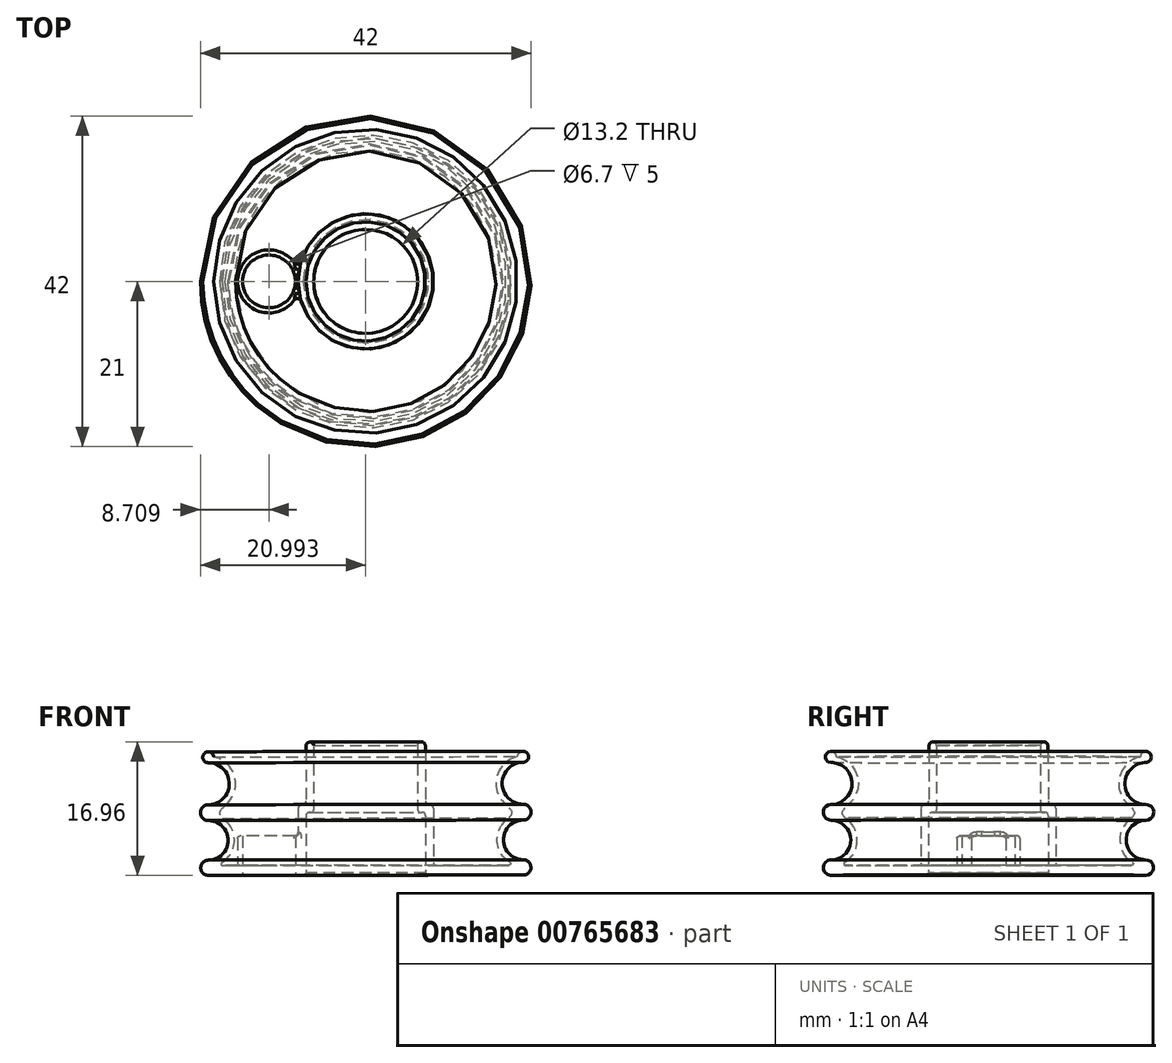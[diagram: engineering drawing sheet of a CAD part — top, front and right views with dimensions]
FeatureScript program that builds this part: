
annotation { "Feature Type Name" : "Feature", "Feature Type Description" : "" }
export const myFeature = defineFeature(function(context is Context, id is Id, definition is map)
    precondition{}
    {
        {
            var Q0;
            Q0=qCreatedBy(makeId("Front.planeOp"),FACE);
            var sketch = newSketch(context, id + "F0", { "sketchPlane" : qUnion([Q0])});
            skLineSegment(sketch, "E0.left", {"start": v(0, 0) * mm, "end": v(-0.02, 15) * mm, "construction": true});
            skLineSegment(sketch, "E0.right", {"start": v(-20, 0) * mm, "end": v(-20.02, 14.31) * mm, "construction": true});
            skLineSegment(sketch, "E1.bottom", {"start": v(-20, 0) * mm, "end": v(-7.61, 0) * mm});
            skLineSegment(sketch, "E1.left", {"start": v(-20, 0) * mm, "end": v(-20.01, 11.57) * mm, "construction": true});
            skLineSegment(sketch, "E2", {"start": v(-7.61, 0) * mm, "end": v(-7.61, 7.57) * mm});
            skPoint(sketch, "E2.endSnap0", {"position": v(-6.61, 7.99) * mm});
            skLineSegment(sketch, "E3", {"start": v(-7.2, 7.99) * mm, "end": v(-6.96, 7.99) * mm});
            skLineSegment(sketch, "E4", {"start": v(-6.62, 16.49) * mm, "end": v(-6.61, 8.34) * mm});
            skArc(sketch, "E5", {"start": v(-20, 0) * mm, "mid": v(-20.97, 0.97) * mm, "end": v(-20, 1.94) * mm});
            skArc(sketch, "E6", {"start": v(-20, 1.94) * mm, "mid": v(-17.5, 4.46) * mm, "end": v(-20, 6.98) * mm});
            skArc(sketch, "E7", {"start": v(-20, 6.98) * mm, "mid": v(-21, 7.97) * mm, "end": v(-20.01, 8.98) * mm});
            skLineSegment(sketch, "E8.4", {"start": v(-7.6, 16.45) * mm, "end": v(-7.6, 9.45) * mm});
            skLineSegment(sketch, "E8.5", {"start": v(-8.15, 8.95) * mm, "end": v(-8.1, 8.95) * mm});
            skLineSegment(sketch, "E8.6", {"start": v(-8.6, 1.25) * mm, "end": v(-8.6, 8.5) * mm});
            skLineSegment(sketch, "E9.0", {"start": v(-19.17, 1.25) * mm, "end": v(-8.6, 1.25) * mm});
            skPoint(sketch, "E10.visualSharp", {"position": v(-7.6, 8.95) * mm});
            skArc(sketch, "E10.filletArc", {"start": v(-8.1, 8.95) * mm, "mid": v(-7.75, 9.1) * mm, "end": v(-7.6, 9.45) * mm});
            skPoint(sketch, "E11.visualSharp", {"position": v(-8.6, 8.95) * mm});
            skArc(sketch, "E11.filletArc", {"start": v(-8.15, 8.95) * mm, "mid": v(-8.47, 8.82) * mm, "end": v(-8.6, 8.5) * mm});
            skArc(sketch, "E12", {"start": v(-20.01, 8.98) * mm, "mid": v(-17.35, 11.65) * mm, "end": v(-20.02, 14.31) * mm});
            skArc(sketch, "E13", {"start": v(-19.32, 15.04) * mm, "mid": v(-20.53, 15.5) * mm, "end": v(-20.02, 14.31) * mm});
            skArc(sketch, "E14.0", {"start": v(-17.85, 8.94) * mm, "mid": v(-16.65, 12.45) * mm, "end": v(-19.32, 15.04) * mm});
            skArc(sketch, "E14.1", {"start": v(-19.17, 1.25) * mm, "mid": v(-16.73, 3.94) * mm, "end": v(-18.22, 7.25) * mm});
            skFitSpline(sketch, "E15", {"points": [v(-17.85, 8.94) * mm, v(-18.6, 7.98) * mm, v(-18.22, 7.25) * mm], "startDerivative": vector(-0.75, -1.37) * mm, "endDerivative": vector(0.7, -1.27) * mm});
            skPoint(sketch, "E16.visualSharp", {"position": v(-7.61, 7.99) * mm});
            skArc(sketch, "E16.filletArc", {"start": v(-7.2, 7.99) * mm, "mid": v(-7.49, 7.86) * mm, "end": v(-7.61, 7.57) * mm});
            skPoint(sketch, "E17.orphan", {"position": v(-6.62, 15.97) * mm});
            skArc(sketch, "E18", {"start": v(-7.6, 16.45) * mm, "mid": v(-7.13, 16.94) * mm, "end": v(-6.62, 16.49) * mm});
            skArc(sketch, "E19.filletArc", {"start": v(-6.96, 7.99) * mm, "mid": v(-6.71, 8.09) * mm, "end": v(-6.61, 8.34) * mm});
            skSolve(sketch);
        }
        {
            var Q0;
            Q0=makeQuery(id+"F0.imprint","IMPRINT",FACE,{"disambiguationData":[TD([[makeQuery(id+"F0.imprint","IMPRINT",EDGE,{"derivedFrom":sQuery(id+"F0.wireOp",EDGE,"E1.bottom")}),1.0]])]});
            var Q1;
            Q1=sQuery(id+"F0.wireOp",EDGE,"E0.left");
            revolve(context, id + "F1", {"surfaceOperationType" : NewSurfaceOperationType.NEW, "entities" : qUnion([Q0]), "axis" : qUnion([Q1]), "revolveType" : RevolveType.FULL});
        }
        {
            var Q0;
            Q0=qCreatedBy(makeId("Top.planeOp"),FACE);
            var sketch = newSketch(context, id + "F2", { "sketchPlane" : qUnion([Q0])});
            skPoint(sketch, "E20", {"position": v(-12.3, 0) * mm});
            skCircle(sketch, "E21", {"center": v(-12.3, 0) * mm, "radius": 4 * mm});
            skSolve(sketch);
        }
        {
            var Q0;
            Q0 = qSketchRegion(id + "F2", true);
            extrude(context, id + "F3", {"entities" : qUnion([Q0]), "operationType" : NewBodyOperationType.ADD, "depth" : 5 * mm, "offsetDistance" : 25 * mm});
        }
        {
            var Q0;
            Q0=sQuery(id+"F2.wireOp",VERTEX,"E20");
            var Q1;
            Q1=makeQuery(id+"F1.opRevolve","SWEPT_BODY",BODY,{"disambiguationData":[OSD([sQuery(id+"F0.wireOp",EDGE,"E1.bottom"),sQuery(id+"F0.wireOp",EDGE,"E2"),sQuery(id+"F0.wireOp",EDGE,"E3"),sQuery(id+"F0.wireOp",EDGE,"E4"),sQuery(id+"F0.wireOp",EDGE,"E5"),sQuery(id+"F0.wireOp",EDGE,"E6"),sQuery(id+"F0.wireOp",EDGE,"E7"),sQuery(id+"F0.wireOp",EDGE,"13a81402-c7b5-4939-9e5f-99af510bba2a"),sQuery(id+"F0.wireOp",EDGE,"ac2dfb1a-4798-471f-8b6a-4aab67035aca"),sQuery(id+"F0.wireOp",EDGE,"E8.0"),sQuery(id+"F0.wireOp",EDGE,"E8.2"),sQuery(id+"F0.wireOp",EDGE,"E8.4"),sQuery(id+"F0.wireOp",EDGE,"E8.5"),sQuery(id+"F0.wireOp",EDGE,"E8.6"),sQuery(id+"F0.wireOp",EDGE,"e1ec032b-aab6-43b8-860a-221fa824a3aa"),sQuery(id+"F0.wireOp",EDGE,"b21e4a9f-9199-4071-8808-4bdfd2212e10"),sQuery(id+"F0.wireOp",EDGE,"E9.0")])]});
            hole(context, id + "F4", {"style" : HoleStyle.SIMPLE, "endStyle" : HoleEndStyle.THROUGH, "oppositeDirection" : true, "holeDiameter" : 6.7 * mm, "majorDiameter" : 5 * mm, "isTappedThrough" : true, "tappedDepth" : 12 * mm, "tapClearance" : 3, "locations" : qUnion([Q0]), "scope" : qUnion([Q1])});
        }
        {
            var Q0;
            Q0=makeQuery(id+"F4.hole-0.boolean.opBoolean","INTERSECT",EDGE,{"derivedFrom":[makeQuery(id+"F3.opExtrude","CAP_FACE",FACE,{"disambiguationData":[OSD([sQuery(id+"F2.wireOp",EDGE,"E21")])],"isStart":false}),makeQuery(id+"F4.hole-0.opRevolve","SWEPT_FACE",FACE,{"disambiguationData":[OSD([sQuery(id+"F4.hole-0.sketch.wireOp",EDGE,"core_line_2")])]})]});
            var Q1;
            Q1=makeQuery(id+"F3.opExtrude","CAP_EDGE",EDGE,{"disambiguationData":[OSD([sQuery(id+"F2.wireOp",EDGE,"E21")])],"isStart":false});
            fillet(context, id + "F5", {"entities" : qUnion([Q0, Q1]), "radius" : 0.31 * mm, "tangentPropagation" : true, "allowEdgeOverflow" : false});
        }
        {
            var Q0;
            Q0=makeQuery(id+"F3.boolean.opBoolean","INTERSECT",EDGE,{"disambiguationData":[OD(0.0)],"derivedFrom":[makeQuery(id+"F1.opRevolve","SWEPT_FACE",FACE,{"disambiguationData":[OSD([sQuery(id+"F0.wireOp",EDGE,"E8.6")])]}),makeQuery(id+"F3.opExtrude","SWEPT_FACE",FACE,{"disambiguationData":[OSD([sQuery(id+"F2.wireOp",EDGE,"E21")])]})]});
            fillet(context, id + "F6", {"entities" : qUnion([Q0]), "radius" : 0.5 * mm, "tangentPropagation" : true, "allowEdgeOverflow" : false});
        }
        {
            var Q0;
            Q0=makeQuery(id+"F1.opRevolve","SWEPT_EDGE",EDGE,{"disambiguationData":[OSD([sQuery(id+"F0.wireOp",EDGE,"E9.0"),sQuery(id+"F0.wireOp",EDGE,"E14.1")])]});
            fillet(context, id + "F7", {"entities" : qUnion([Q0]), "radius" : 0.2 * mm, "tangentPropagation" : true, "allowEdgeOverflow" : false});
        }
        {
            var Q0;
            Q0=makeQuery(id+"F1.opRevolve","SWEPT_EDGE",EDGE,{"disambiguationData":[OSD([sQuery(id+"F0.wireOp",EDGE,"E1.bottom"),sQuery(id+"F0.wireOp",EDGE,"E2")])]});
            chamfer(context, id + "F8", {"entities" : qUnion([Q0]), "width" : 0.3 * mm, "tangentPropagation" : true});
        }
    });
